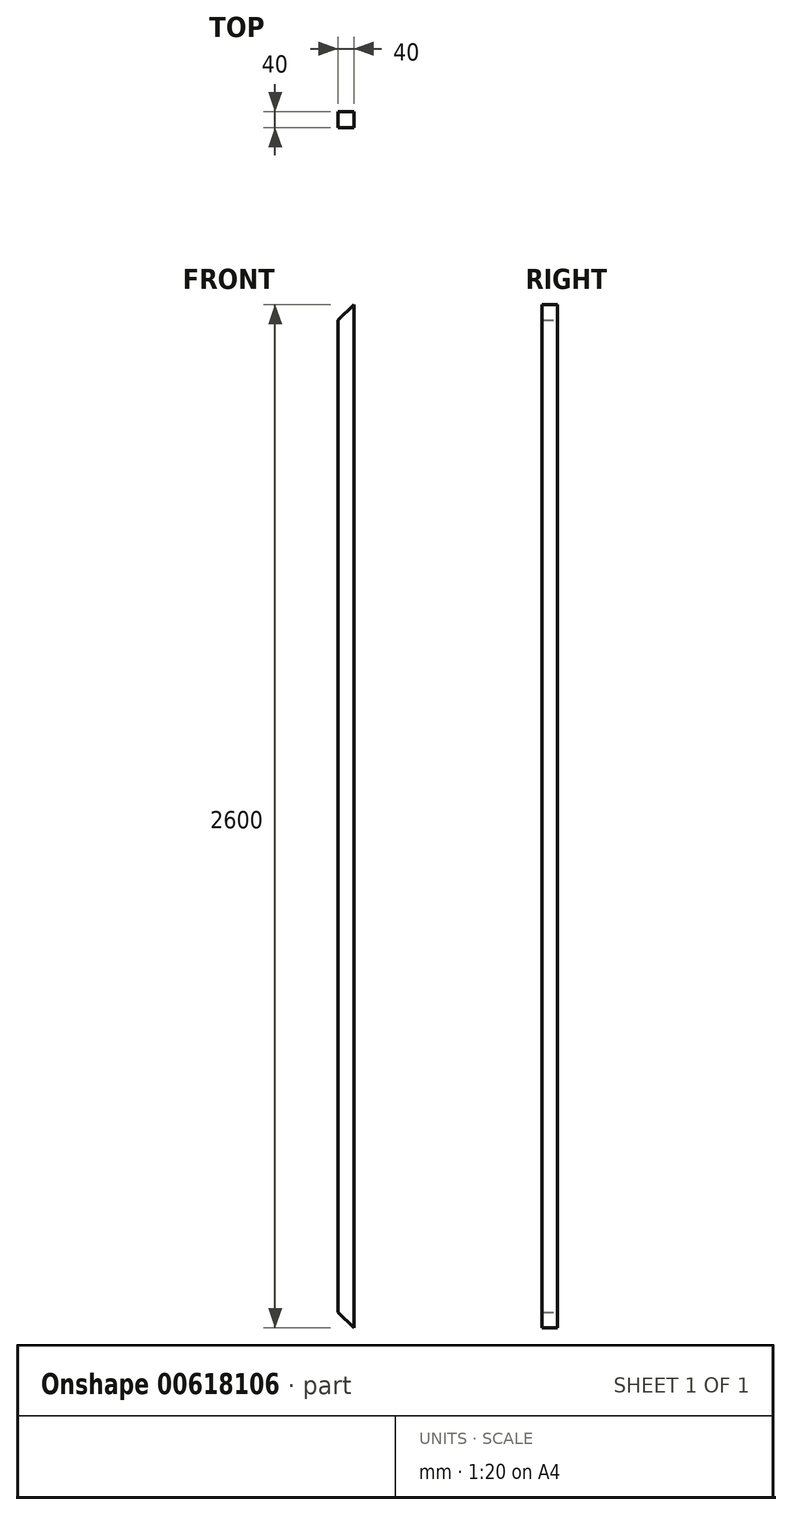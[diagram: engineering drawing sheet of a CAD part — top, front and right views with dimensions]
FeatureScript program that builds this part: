
annotation { "Feature Type Name" : "Feature", "Feature Type Description" : "" }
export const myFeature = defineFeature(function(context is Context, id is Id, definition is map)
    precondition{}
    {
        {
            var Q0;
            Q0=qCreatedBy(makeId("Front.planeOp"),FACE);
            var sketch = newSketch(context, id + "F0", { "sketchPlane" : qUnion([Q0])});
            skLineSegment(sketch, "E0.left", {"start": v(20, -1300) * mm, "end": v(20, 1300) * mm});
            skLineSegment(sketch, "E0.right", {"start": v(-20, -1260) * mm, "end": v(-20, 1260) * mm});
            skPoint(sketch, "E0.middle", {"position": v(0, 0) * mm});
            skLineSegment(sketch, "E1", {"start": v(-20, 1260) * mm, "end": v(20, 1300) * mm});
            skPoint(sketch, "E2", {"position": v(-20, 1260) * mm});
            skLineSegment(sketch, "E3", {"start": v(20, -1300) * mm, "end": v(-20, -1260) * mm});
            skPoint(sketch, "E4.end.orphan", {"position": v(20, 1260) * mm});
            skSolve(sketch);
        }
        {
            var Q0;
            Q0 = qSketchRegion(id + "F0", true);
            extrude(context, id + "F1", {"entities" : qUnion([Q0]), "depth" : 40 * mm, "offsetDistance" : 25 * mm});
        }
    });
